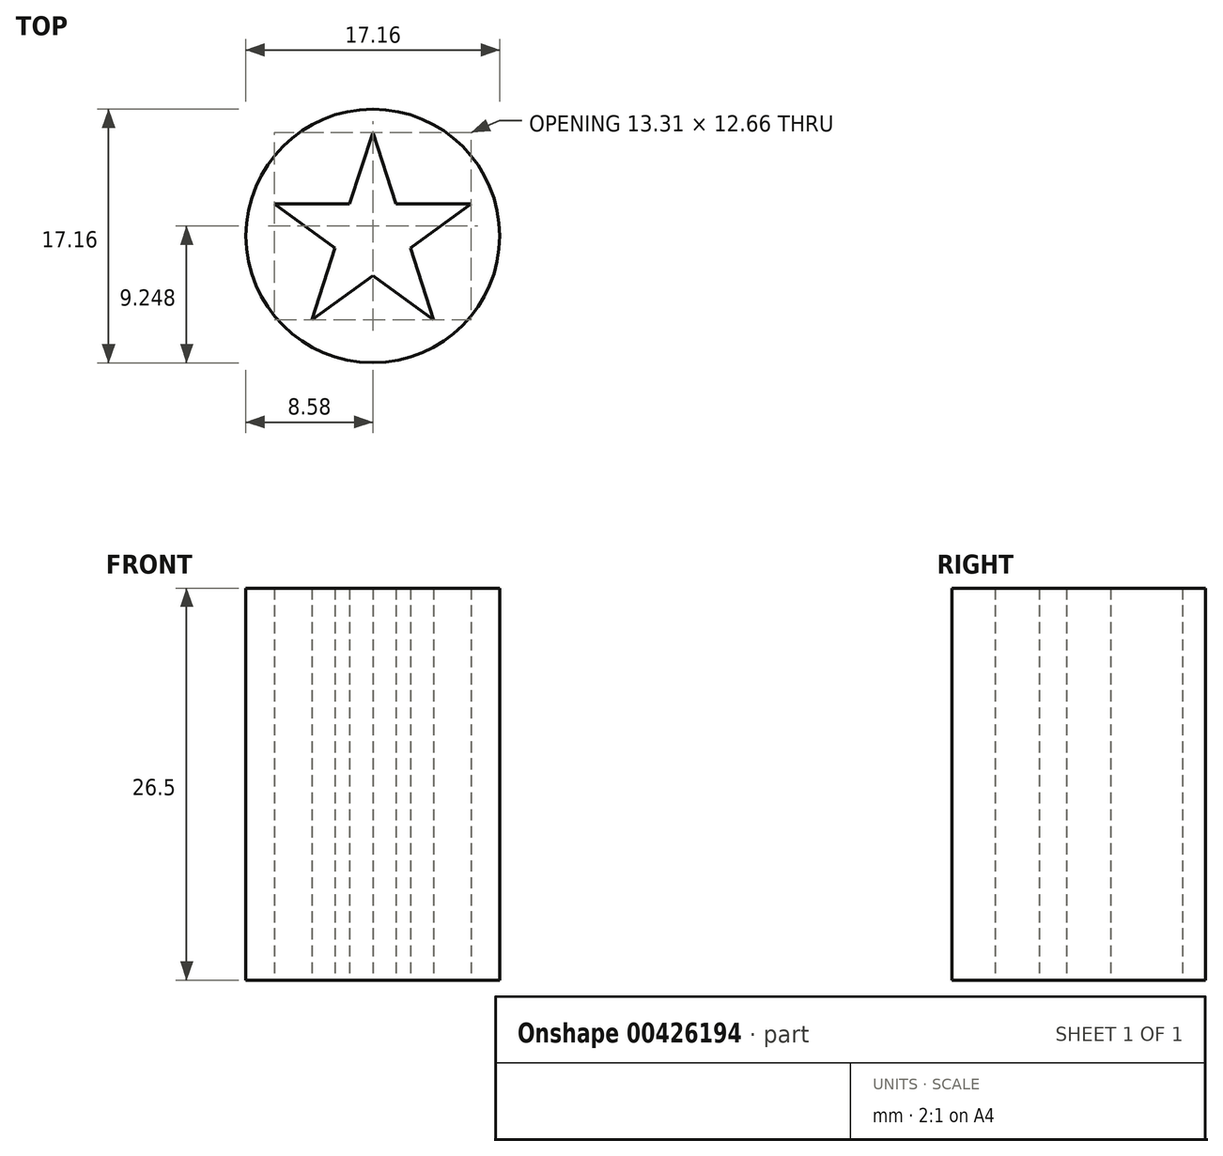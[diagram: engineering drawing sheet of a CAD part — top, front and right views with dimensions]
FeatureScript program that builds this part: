
annotation { "Feature Type Name" : "Feature", "Feature Type Description" : "" }
export const myFeature = defineFeature(function(context is Context, id is Id, definition is map)
    precondition{}
    {
        {
            var Q0;
            Q0=qCreatedBy(makeId("Top.planeOp"),FACE);
            var sketch = newSketch(context, id + "F0", { "sketchPlane" : qUnion([Q0])});
            skCircle(sketch, "E0", {"center": v(0, 0) * mm, "radius": 8.57 * mm});
            skSolve(sketch);
        }
        {
            var Q0;
            Q0=qSketchRegion(id+"F0",true);
            extrude(context, id + "F1", {"entities" : qUnion([Q0]), "depth" : 26.5 * mm});
        }
        {
            var Q0;
            Q0=makeQuery(id+"F1.opExtrude","CAP_FACE",FACE,{"disambiguationData":[OSD([sQuery(id+"F0.wireOp",EDGE,"E0")])],"isStart":true});
            var sketch = newSketch(context, id + "F2", { "sketchPlane" : qUnion([Q0])});
            skCircle(sketch, "E1.cCircle", {"center": v(0, 0) * mm, "radius": 7 * mm, "construction": true});
            skLineSegment(sketch, "E1.0", {"start": v(0, -7) * mm, "end": v(-6.66, -2.16) * mm, "construction": true});
            skLineSegment(sketch, "E1.1", {"start": v(-6.66, -2.16) * mm, "end": v(-4.11, 5.66) * mm, "construction": true});
            skLineSegment(sketch, "E1.2", {"start": v(-4.11, 5.66) * mm, "end": v(4.11, 5.66) * mm, "construction": true});
            skLineSegment(sketch, "E1.3", {"start": v(4.11, 5.66) * mm, "end": v(6.66, -2.16) * mm, "construction": true});
            skLineSegment(sketch, "E1.4", {"start": v(6.66, -2.16) * mm, "end": v(0, -7) * mm, "construction": true});
            skLineSegment(sketch, "E2", {"start": v(-4.11, 5.66) * mm, "end": v(0, -7) * mm});
            skLineSegment(sketch, "E3", {"start": v(0, -7) * mm, "end": v(4.11, 5.66) * mm});
            skLineSegment(sketch, "E4", {"start": v(4.11, 5.66) * mm, "end": v(-6.66, -2.16) * mm});
            skLineSegment(sketch, "E5", {"start": v(-6.66, -2.16) * mm, "end": v(6.66, -2.16) * mm});
            skLineSegment(sketch, "E6", {"start": v(6.66, -2.16) * mm, "end": v(-4.11, 5.66) * mm});
            skSolve(sketch);
        }
        {
            var Q0;
            {var subQ0=sQuery(id+"F2.wireOp",EDGE,"E6");var subQ1=sQuery(id+"F2.wireOp",EDGE,"E2");var subQ2=makeQuery(id+"F2.imprint","INTERSECT",VERTEX,{"derivedFrom":[subQ1,subQ0]});Q0=makeQuery(id+"F2.imprint","IMPRINT",FACE,{"disambiguationData":[TD([[makeQuery(id+"F2.imprint","IMPRINT",EDGE,{"disambiguationData":[TD([[subQ2,-1.0]])],"derivedFrom":subQ1}),1.0]])]});}
            var Q1;
            {var subQ0=sQuery(id+"F2.wireOp",EDGE,"E4");var subQ1=sQuery(id+"F2.wireOp",EDGE,"E2");var subQ2=makeQuery(id+"F2.imprint","INTERSECT",VERTEX,{"derivedFrom":[subQ1,subQ0]});Q1=makeQuery(id+"F2.imprint","IMPRINT",FACE,{"disambiguationData":[TD([[makeQuery(id+"F2.imprint","IMPRINT",EDGE,{"disambiguationData":[TD([[subQ2,-1.0]])],"derivedFrom":subQ1}),-1.0]])]});}
            var Q2;
            {var subQ0=sQuery(id+"F2.wireOp",EDGE,"E3");var subQ1=sQuery(id+"F2.wireOp",EDGE,"E2");var subQ2=makeQuery(id+"F2.imprint","INTERSECT",VERTEX,{"derivedFrom":[subQ1,subQ0]});Q2=makeQuery(id+"F2.imprint","IMPRINT",FACE,{"disambiguationData":[TD([[makeQuery(id+"F2.imprint","IMPRINT",EDGE,{"disambiguationData":[TD([[subQ2,1.0]])],"derivedFrom":subQ1}),1.0]])]});}
            var Q3;
            {var subQ0=sQuery(id+"F2.wireOp",EDGE,"E5");var subQ1=sQuery(id+"F2.wireOp",EDGE,"E3");var subQ2=makeQuery(id+"F2.imprint","INTERSECT",VERTEX,{"derivedFrom":[subQ1,subQ0]});Q3=makeQuery(id+"F2.imprint","IMPRINT",FACE,{"disambiguationData":[TD([[makeQuery(id+"F2.imprint","IMPRINT",EDGE,{"disambiguationData":[TD([[subQ2,-1.0]])],"derivedFrom":subQ1}),-1.0]])]});}
            var Q4;
            {var subQ0=sQuery(id+"F2.wireOp",EDGE,"E4");var subQ1=sQuery(id+"F2.wireOp",EDGE,"E3");var subQ2=makeQuery(id+"F2.imprint","INTERSECT",VERTEX,{"derivedFrom":[subQ1,subQ0]});Q4=makeQuery(id+"F2.imprint","IMPRINT",FACE,{"disambiguationData":[TD([[makeQuery(id+"F2.imprint","IMPRINT",EDGE,{"disambiguationData":[TD([[subQ2,1.0]])],"derivedFrom":subQ1}),1.0]])]});}
            var Q5;
            {var subQ1=sQuery(id+"F2.wireOp",EDGE,"E2");var subQ5=sQuery(id+"F2.wireOp",EDGE,"E4");var subQ6=makeQuery(id+"F2.imprint","INTERSECT",VERTEX,{"derivedFrom":[subQ1,subQ5]});Q5=makeQuery(id+"F2.imprint","IMPRINT",FACE,{"disambiguationData":[TD([[makeQuery(id+"F2.imprint","IMPRINT",EDGE,{"disambiguationData":[TD([[subQ6,-1.0]])],"derivedFrom":subQ1}),1.0]])]});}
            extrude(context, id + "F3", {"entities" : qUnion([Q0, Q1, Q2, Q3, Q4, Q5]), "operationType" : NewBodyOperationType.REMOVE, "oppositeDirection" : true, "depth" : 26.5 * mm});
        }
    });
